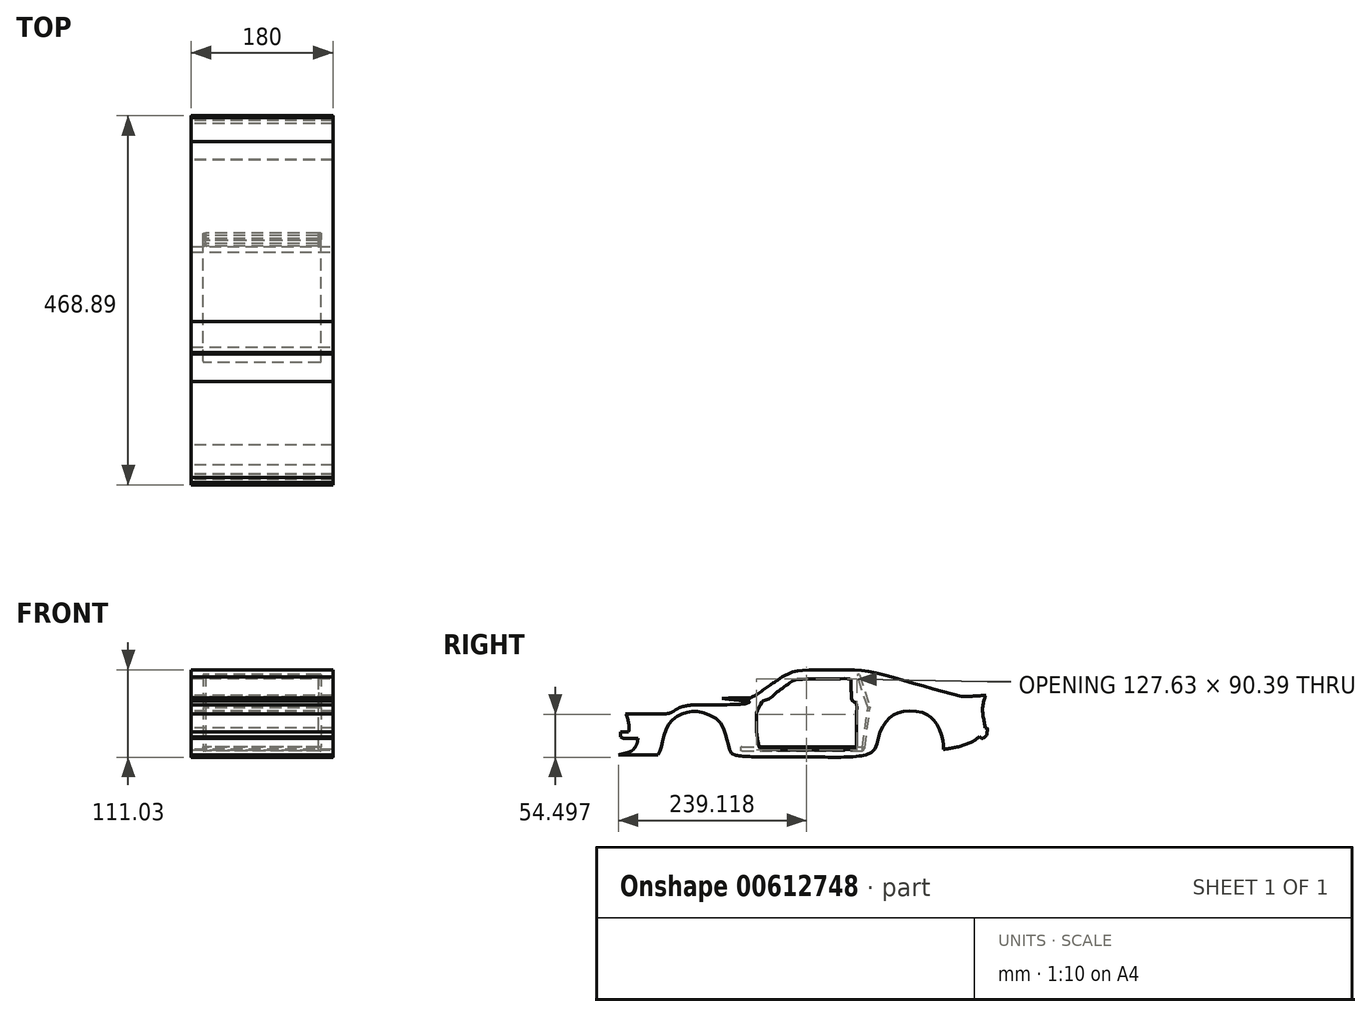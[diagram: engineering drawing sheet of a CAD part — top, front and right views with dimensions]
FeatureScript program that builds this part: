
annotation { "Feature Type Name" : "Feature", "Feature Type Description" : "" }
export const myFeature = defineFeature(function(context is Context, id is Id, definition is map)
    precondition{}
    {
        {
            var Q0;
            Q0=qCreatedBy(makeId("Right.planeOp"),FACE);
            var sketch = newSketch(context, id + "F0", { "sketchPlane" : qUnion([Q0])});
            skLineSegment(sketch, "E0", {"start": v(34.5, 1.2) * mm, "end": v(34.5, 56.2) * mm});
            skLineSegment(sketch, "E1", {"start": v(34.5, 56.2) * mm, "end": v(34.5, -53.8) * mm});
            skFitSpline(sketch, "E2", {"points": [v(-192.02, 5.62) * mm, v(-188.23, -1.97) * mm, v(-186.33, -8.9) * mm, v(-185.33, -17.74) * mm, v(-186.06, -22.02) * mm], "startDerivative": vector(14.34, -26.77) * mm, "endDerivative": vector(-3.15, -14.8) * mm});
            skLineSegment(sketch, "E3", {"start": v(-186.06, -22.02) * mm, "end": v(-150.06, -22.02) * mm});
            skLineSegment(sketch, "E4", {"start": v(-186.06, -22.02) * mm, "end": v(-196.06, -22.02) * mm});
            skLineSegment(sketch, "E5", {"start": v(-196.06, -22.02) * mm, "end": v(-196.06, -28.02) * mm});
            skLineSegment(sketch, "E6", {"start": v(-196.06, -28.02) * mm, "end": v(-192.6, -30.02) * mm});
            skLineSegment(sketch, "E7", {"start": v(-192.6, -30.02) * mm, "end": v(-152.6, -30.02) * mm});
            skFitSpline(sketch, "E8", {"points": [v(-189.69, 1.2) * mm, v(-143.65, 1.2) * mm, v(-132.51, 2.57) * mm, v(-124.9, 7.2) * mm, v(-118.52, 10.02) * mm, v(-106.8, 12.25) * mm, v(-95.05, 12.73) * mm, v(-67.03, 12.66) * mm, v(-45.8, 13.3) * mm, v(-38.33, 13.95) * mm, v(-33.02, 16.11) * mm, v(-30.86, 21.5) * mm], "startDerivative": vector(365.59, 0) * mm, "endDerivative": vector(6.51, 98.79) * mm});
            skLineSegment(sketch, "E9", {"start": v(-32.83, 21.62) * mm, "end": v(-30.86, 21.5) * mm});
            skLineSegment(sketch, "E10", {"start": v(-148.82, -50.9) * mm, "end": v(-203.82, -50.9) * mm});
            skFitSpline(sketch, "E11", {"points": [v(-203.82, -50.9) * mm, v(-201.8, -50.97) * mm, v(-195.54, -50.07) * mm, v(-184.25, -46.94) * mm, v(-179.78, -43.7) * mm, v(-175.75, -37.77) * mm, v(-174.19, -30.02) * mm], "startDerivative": vector(14.97, 20.7) * mm, "endDerivative": vector(5.44, 44.14) * mm});
            skFitSpline(sketch, "E12", {"points": [v(-192.6, -30.02) * mm, v(-190.74, -34.42) * mm, v(-187.5, -41.24) * mm, v(-184.25, -46.94) * mm], "startDerivative": vector(3.9, -14.04) * mm, "endDerivative": vector(12.4, -22.87) * mm});
            skFitSpline(sketch, "E13", {"points": [v(-191.23, -30.02) * mm, v(-189.5, -34.04) * mm, v(-185.58, -40.09) * mm, v(-179.78, -43.7) * mm], "startDerivative": vector(6.31, -12.78) * mm, "endDerivative": vector(21.2, -4.61) * mm});
            skFitSpline(sketch, "E14", {"points": [v(-173.44, -22.02) * mm, v(-172.32, -17.3) * mm, v(-173.44, -10.15) * mm, v(-176.23, -2.55) * mm, v(-178.58, 1.2) * mm], "startDerivative": vector(6.87, 20.01) * mm, "endDerivative": vector(-11.1, 15.63) * mm});
            skFitSpline(sketch, "E15", {"points": [v(-164.83, -22.02) * mm, v(-161.47, -19.43) * mm, v(-159.12, -13.17) * mm, v(-159.24, -5.46) * mm, v(-160.13, 1.18) * mm], "startDerivative": vector(17.5, 10.07) * mm, "endDerivative": vector(-3.71, 25.15) * mm});
            skFitSpline(sketch, "E16", {"points": [v(-148.82, -50.9) * mm, v(-144.92, -43.03) * mm, v(-142.13, -29.94) * mm, v(-136.76, -14.85) * mm, v(-126.59, -3.44) * mm, v(-114.17, 2.26) * mm, v(-102.43, 4.27) * mm, v(-84.65, 0.36) * mm, v(-69.45, -10.71) * mm, v(-62.3, -26.37) * mm, v(-59.38, -38.44) * mm, v(-56.36, -47.83) * mm, v(-45.3, -52.3) * mm, v(-13.05, -53.35) * mm, v(7.6, -53.58) * mm], "startDerivative": vector(73.15, 160.48) * mm, "endDerivative": vector(240.73, -3.86) * mm});
            skFitSpline(sketch, "E17", {"points": [v(213.63, -43.94) * mm, v(234.09, -40.23) * mm, v(253.22, -32.62) * mm, v(262, -26.18) * mm, v(266.1, -24.23) * mm, v(266.88, -17) * mm, v(265.12, -6.27) * mm, v(263.56, 7.6) * mm, v(265.71, 19.51) * mm, v(267.62, 24.74) * mm], "startDerivative": vector(137.64, 17.09) * mm, "endDerivative": vector(24.1, 59.58) * mm});
            skFitSpline(sketch, "E18", {"points": [v(266.88, -17) * mm, v(265.12, -17) * mm, v(262.4, -17) * mm, v(258.68, -17) * mm, v(257.15, -18.37) * mm, v(257.15, -21.73) * mm, v(258.3, -25.76) * mm, v(260.84, -28.8) * mm, v(262.9, -30.02) * mm, v(265.77, -28.87) * mm, v(268.4, -26.17) * mm, v(269.3, -22.64) * mm, v(269.3, -17) * mm, v(266.88, -17) * mm]});
            skFitSpline(sketch, "E19", {"points": [v(7.6, -53.58) * mm, v(26.53, -53.46) * mm, v(61.93, -53.8) * mm, v(115.2, -50.9) * mm, v(127.52, -41.9) * mm, v(133.08, -22.93) * mm, v(142.48, -7.27) * mm, v(153.5, 1.2) * mm, v(169.34, 5.17) * mm, v(191.58, 1.2) * mm, v(199.59, -5.06) * mm, v(207.48, -15.62) * mm, v(213.05, -32.57) * mm, v(213.63, -43.94) * mm], "startDerivative": vector(235.53, -2.28) * mm, "endDerivative": vector(-18.69, -186.2) * mm});
            skFitSpline(sketch, "E20", {"points": [v(-30.86, 21.5) * mm, v(-26.93, 19.51) * mm, v(-23.3, 19.33) * mm, v(-19.78, 19.51) * mm, v(-16.02, 21.5) * mm, v(10.62, 41.85) * mm, v(14.97, 44.81) * mm, v(15.38, 46.5) * mm, v(13.58, 47.43) * mm, v(8.48, 47.77) * mm], "startDerivative": vector(38.14, -25.76) * mm, "endDerivative": vector(-51.85, 1.69) * mm});
            skFitSpline(sketch, "E21", {"points": [v(-15.26, 17.54) * mm, v(-19.76, 11.3) * mm, v(-23.08, 3.29) * mm, v(-23.86, -5.7) * mm, v(-23.47, -19.36) * mm, v(-22.3, -29.9) * mm, v(-21.12, -37.12) * mm, v(-19.76, -42.4) * mm, v(-11.17, -44.15) * mm, v(14.6, -44.54) * mm, v(53.99, -44.53) * mm, v(82.73, -44.34) * mm, v(98.09, -43.75) * mm, v(102.52, -41.2) * mm, v(103.54, -32.58) * mm, v(103.6, 5.18) * mm, v(102.56, 15.34) * mm, v(98.37, 17.49) * mm, v(96.74, 26.5) * mm, v(96.66, 36.35) * mm, v(96.66, 42.91) * mm, v(95.68, 44.96) * mm, v(81.56, 45.78) * mm, v(56.6, 45.62) * mm, v(29.28, 44.8) * mm, v(21.8, 42.75) * mm, v(11.47, 35.2) * mm, v(0.72, 27.32) * mm, v(-8.64, 19.69) * mm, v(-15.26, 17.54) * mm]});
            skFitSpline(sketch, "E22", {"points": [v(8.48, 47.77) * mm, v(14.97, 51.2) * mm, v(26.65, 55.33) * mm, v(46.94, 56.85) * mm, v(97.46, 56.85) * mm, v(127.97, 53.26) * mm, v(181.98, 38.26) * mm, v(236.6, 23.3) * mm], "startDerivative": vector(84.82, 47.6) * mm, "endDerivative": vector(279.07, -65.23) * mm});
            skFitSpline(sketch, "E23", {"points": [v(8.48, 47.77) * mm, v(1.78, 43.11) * mm, v(-5.74, 38.1) * mm, v(-14.94, 31.55) * mm, v(-24.27, 25.14) * mm, v(-30.86, 21.5) * mm], "startDerivative": vector(-35.57, -25.23) * mm, "endDerivative": vector(-34.63, -24.08) * mm});
            skArc(sketch, "E24", {"start": v(224.04, -42.4) * mm, "mid": v(171.31, 15.22) * mm, "end": v(119.33, -43.08) * mm});
            skLineSegment(sketch, "E25", {"start": v(119.33, -43.08) * mm, "end": v(115.2, -50.9) * mm});
            skArc(sketch, "E26", {"start": v(-49.73, -51.5) * mm, "mid": v(-98.4, 12.55) * mm, "end": v(-153.36, -46.19) * mm});
            skLineSegment(sketch, "E27", {"start": v(-153.36, -46.19) * mm, "end": v(-148.82, -50.9) * mm});
            skFitSpline(sketch, "E28", {"points": [v(-192.02, 5.62) * mm, v(-171.85, 12.08) * mm, v(-144.7, 17.14) * mm, v(-106.6, 19.87) * mm, v(-67.7, 20.83) * mm, v(-46.55, 21.45) * mm, v(-32.83, 21.62) * mm], "startDerivative": vector(129.5, 46.92) * mm, "endDerivative": vector(108.9, 1.61) * mm});
            skLineSegment(sketch, "E29", {"start": v(-15.26, 17.54) * mm, "end": v(-31.31, 19.04) * mm});
            skFitSpline(sketch, "E30", {"points": [v(267.62, 24.74) * mm, v(236.6, 23.3) * mm, v(154.17, 23.3) * mm, v(117.95, 18.48) * mm, v(68.92, 14.9) * mm, v(0.95, 15.46) * mm, v(-67.7, 20.83) * mm], "startDerivative": vector(-203.68, -16.4) * mm, "endDerivative": vector(-404.49, 46.26) * mm});
            skLineSegment(sketch, "E31", {"start": v(-67.7, 20.83) * mm, "end": v(-32.83, 21.62) * mm});
            skLineSegment(sketch, "E32", {"start": v(117.27, -47) * mm, "end": v(-48.93, -47) * mm});
            skLineSegment(sketch, "E33", {"start": v(240.83, 54.27) * mm, "end": v(272.77, 56.66) * mm});
            skLineSegment(sketch, "E34", {"start": v(272.77, 56.66) * mm, "end": v(264.67, 50.23) * mm});
            skLineSegment(sketch, "E35", {"start": v(264.67, 50.23) * mm, "end": v(242.9, 50.23) * mm});
            skLineSegment(sketch, "E36", {"start": v(242.9, 50.23) * mm, "end": v(240.83, 54.27) * mm});
            skLineSegment(sketch, "E37", {"start": v(236.6, 23.3) * mm, "end": v(253.78, 55.24) * mm});
            skPoint(sketch, "E37.endSnap0", {"position": v(253.78, 50.23) * mm});
            skLineSegment(sketch, "E38", {"start": v(246.23, 23.46) * mm, "end": v(263.74, 55.99) * mm});
            skLineSegment(sketch, "E39", {"start": v(-192.02, 5.62) * mm, "end": v(-213.66, -3) * mm});
            skSolve(sketch);
        }
        {
            var Q0;
            {var subQ0=sQuery(id+"F0.wireOp",EDGE,"E15");Q0=makeQuery(id+"F0.imprint","IMPRINT",FACE,{"disambiguationData":[TD([[makeQuery(id+"F0.imprint","IMPRINT",EDGE,{"derivedFrom":subQ0}),-1.0]])]});}
            var Q1;
            {var subQ0=sQuery(id+"F0.wireOp",EDGE,"E14");Q1=makeQuery(id+"F0.imprint","IMPRINT",FACE,{"disambiguationData":[TD([[makeQuery(id+"F0.imprint","IMPRINT",EDGE,{"derivedFrom":subQ0}),-1.0]])]});}
            var Q2;
            {var subQ0=sQuery(id+"F0.wireOp",EDGE,"E4");Q2=makeQuery(id+"F0.imprint","IMPRINT",FACE,{"disambiguationData":[TD([[makeQuery(id+"F0.imprint","IMPRINT",EDGE,{"derivedFrom":subQ0}),1.0]])]});}
            var Q3;
            {var subQ5=sQuery(id+"F0.wireOp",EDGE,"E21");var subQ6=sQuery(id+"F0.wireOp",EDGE,"E1");var subQ7=makeQuery(id+"F0.imprint","INTERSECT",VERTEX,{"disambiguationData":[OD(1.0)],"derivedFrom":[subQ6,subQ5]});Q3=makeQuery(id+"F0.imprint","IMPRINT",FACE,{"disambiguationData":[TD([[makeQuery(id+"F0.imprint","IMPRINT",EDGE,{"disambiguationData":[TD([[subQ7,-1.0]])],"derivedFrom":subQ6}),-1.0]])]});}
            var Q4;
            {var subQ0=sQuery(id+"F0.wireOp",EDGE,"E1");var subQ1=makeQuery(id+"F0.imprint","IMPRINT",VERTEX,{"derivedFrom":subQ0});Q4=makeQuery(id+"F0.imprint","IMPRINT",FACE,{"disambiguationData":[TD([[makeQuery(id+"F0.imprint","IMPRINT",EDGE,{"disambiguationData":[TD([[subQ1,1.0]])],"derivedFrom":subQ0}),-1.0]])]});}
            var Q5;
            {var subQ0=sQuery(id+"F0.wireOp",EDGE,"E1");var subQ1=makeQuery(id+"F0.imprint","IMPRINT",VERTEX,{"derivedFrom":subQ0});Q5=makeQuery(id+"F0.imprint","IMPRINT",FACE,{"disambiguationData":[TD([[makeQuery(id+"F0.imprint","IMPRINT",EDGE,{"disambiguationData":[TD([[subQ1,1.0]])],"derivedFrom":subQ0}),1.0]])]});}
            var Q6;
            {var subQ0=sQuery(id+"F0.wireOp",EDGE,"E19");var subQ1=sQuery(id+"F0.wireOp",EDGE,"E1");var subQ2=makeQuery(id+"F0.imprint","INTERSECT",VERTEX,{"derivedFrom":[subQ1,subQ0]});Q6=makeQuery(id+"F0.imprint","IMPRINT",FACE,{"disambiguationData":[TD([[makeQuery(id+"F0.imprint","IMPRINT",EDGE,{"disambiguationData":[TD([[subQ2,1.0]])],"derivedFrom":subQ1}),1.0]])]});}
            var Q7;
            {var subQ5=sQuery(id+"F0.wireOp",EDGE,"E19");var subQ7=sQuery(id+"F0.wireOp",EDGE,"E1");var subQ8=makeQuery(id+"F0.imprint","INTERSECT",VERTEX,{"derivedFrom":[subQ7,subQ5]});Q7=makeQuery(id+"F0.imprint","IMPRINT",FACE,{"disambiguationData":[TD([[makeQuery(id+"F0.imprint","IMPRINT",EDGE,{"disambiguationData":[TD([[subQ8,1.0]])],"derivedFrom":subQ7}),-1.0]])]});}
            var Q8;
            {var subQ11=sQuery(id+"F0.wireOp",EDGE,"E24");Q8=makeQuery(id+"F0.imprint","IMPRINT",FACE,{"disambiguationData":[TD([[makeQuery(id+"F0.imprint","IMPRINT",EDGE,{"derivedFrom":subQ11}),-1.0]])]});}
            var Q9;
            {var subQ5=sQuery(id+"F0.wireOp",EDGE,"E20");Q9=makeQuery(id+"F0.imprint","IMPRINT",FACE,{"disambiguationData":[TD([[makeQuery(id+"F0.imprint","IMPRINT",EDGE,{"derivedFrom":subQ5}),-1.0]])]});}
            var Q10;
            {var subQ0=sQuery(id+"F0.wireOp",EDGE,"E21");var subQ1=sQuery(id+"F0.wireOp",EDGE,"E1");var subQ2=makeQuery(id+"F0.imprint","INTERSECT",VERTEX,{"disambiguationData":[OD(0.0)],"derivedFrom":[subQ1,subQ0]});Q10=makeQuery(id+"F0.imprint","IMPRINT",FACE,{"disambiguationData":[TD([[makeQuery(id+"F0.imprint","IMPRINT",EDGE,{"disambiguationData":[TD([[subQ2,-1.0]])],"derivedFrom":subQ1}),1.0]])]});}
            var Q11;
            {var subQ4=sQuery(id+"F0.wireOp",EDGE,"E9");Q11=makeQuery(id+"F0.imprint","IMPRINT",FACE,{"disambiguationData":[TD([[makeQuery(id+"F0.imprint","IMPRINT",EDGE,{"derivedFrom":subQ4}),-1.0]])]});}
            var Q12;
            {var subQ0=sQuery(id+"F0.wireOp",EDGE,"E21");var subQ1=sQuery(id+"F0.wireOp",EDGE,"E1");var subQ2=makeQuery(id+"F0.imprint","INTERSECT",VERTEX,{"disambiguationData":[OD(0.0)],"derivedFrom":[subQ1,subQ0]});Q12=makeQuery(id+"F0.imprint","IMPRINT",FACE,{"disambiguationData":[TD([[makeQuery(id+"F0.imprint","IMPRINT",EDGE,{"disambiguationData":[TD([[subQ2,-1.0]])],"derivedFrom":subQ1}),-1.0]])]});}
            var Q13;
            {var subQ0=sQuery(id+"F0.wireOp",EDGE,"E18");var subQ1=sQuery(id+"F0.wireOp",EDGE,"E17");var subQ2=makeQuery(id+"F0.imprint","INTERSECT",VERTEX,{"disambiguationData":[OD(0.0)],"derivedFrom":[subQ1,subQ0]});Q13=makeQuery(id+"F0.imprint","IMPRINT",FACE,{"disambiguationData":[TD([[makeQuery(id+"F0.imprint","IMPRINT",EDGE,{"disambiguationData":[TD([[subQ2,-1.0]])],"derivedFrom":subQ1}),1.0]])]});}
            var Q14;
            {var subQ0=sQuery(id+"F0.wireOp",EDGE,"E18");var subQ1=sQuery(id+"F0.wireOp",EDGE,"E17");var subQ2=makeQuery(id+"F0.imprint","INTERSECT",VERTEX,{"disambiguationData":[OD(0.0)],"derivedFrom":[subQ1,subQ0]});Q14=makeQuery(id+"F0.imprint","IMPRINT",FACE,{"disambiguationData":[TD([[makeQuery(id+"F0.imprint","IMPRINT",EDGE,{"disambiguationData":[TD([[subQ2,-1.0]])],"derivedFrom":subQ1}),-1.0]])]});}
            var Q15;
            {var subQ0=sQuery(id+"F0.wireOp",EDGE,"E29");Q15=makeQuery(id+"F0.imprint","IMPRINT",FACE,{"disambiguationData":[TD([[makeQuery(id+"F0.imprint","IMPRINT",EDGE,{"derivedFrom":subQ0}),1.0]])]});}
            var Q16;
            {var subQ5=sQuery(id+"F0.wireOp",EDGE,"E27");Q16=makeQuery(id+"F0.imprint","IMPRINT",FACE,{"disambiguationData":[TD([[makeQuery(id+"F0.imprint","IMPRINT",EDGE,{"derivedFrom":subQ5}),-1.0]])]});}
            var Q17;
            {var subQ4=sQuery(id+"F0.wireOp",EDGE,"E27");Q17=makeQuery(id+"F0.imprint","IMPRINT",FACE,{"disambiguationData":[TD([[makeQuery(id+"F0.imprint","IMPRINT",EDGE,{"derivedFrom":subQ4}),1.0]])]});}
            var Q18;
            {var subQ0=sQuery(id+"F0.wireOp",EDGE,"E24");Q18=makeQuery(id+"F0.imprint","IMPRINT",FACE,{"disambiguationData":[TD([[makeQuery(id+"F0.imprint","IMPRINT",EDGE,{"derivedFrom":subQ0}),1.0]])]});}
            var Q19;
            {var subQ9=sQuery(id+"F0.wireOp",EDGE,"E28");Q19=makeQuery(id+"F0.imprint","IMPRINT",FACE,{"disambiguationData":[TD([[makeQuery(id+"F0.imprint","IMPRINT",EDGE,{"derivedFrom":subQ9}),-1.0]])]});}
            var Q20;
            {var subQ5=sQuery(id+"F0.wireOp",EDGE,"E14");Q20=makeQuery(id+"F0.imprint","IMPRINT",FACE,{"disambiguationData":[TD([[makeQuery(id+"F0.imprint","IMPRINT",EDGE,{"derivedFrom":subQ5}),1.0]])]});}
            var Q21;
            {var subQ0=sQuery(id+"F0.wireOp",EDGE,"E26");var subQ1=sQuery(id+"F0.wireOp",EDGE,"E8");var subQ2=makeQuery(id+"F0.imprint","INTERSECT",VERTEX,{"disambiguationData":[OD(1.0)],"derivedFrom":[subQ1,subQ0]});Q21=makeQuery(id+"F0.imprint","IMPRINT",FACE,{"disambiguationData":[TD([[makeQuery(id+"F0.imprint","IMPRINT",EDGE,{"disambiguationData":[TD([[subQ2,-1.0]])],"derivedFrom":subQ1}),-1.0]])]});}
            var Q22;
            Q22=makeQuery(id+"F0.imprint","IMPRINT",FACE,{"disambiguationData":[TD([[makeQuery(id+"F0.imprint","IMPRINT",EDGE,{"derivedFrom":sQuery(id+"F0.wireOp",EDGE,"E20")}),1.0]])]});
            extrude(context, id + "F1", {"entities" : qUnion([Q0, Q1, Q2, Q3, Q4, Q5, Q6, Q7, Q8, Q9, Q10, Q11, Q12, Q13, Q14, Q15, Q16, Q17, Q18, Q19, Q20, Q21, Q22]), "endBound" : BoundingType.SYMMETRIC, "depth" : 180 * mm, "offsetDistance" : 25 * mm});
        }
        {
            var Q0;
            Q0=qCreatedBy(makeId("Right.planeOp"),FACE);
            var sketch = newSketch(context, id + "F2", { "sketchPlane" : qUnion([Q0])});
            skLineSegment(sketch, "E40.bottom", {"start": v(-43.54, -46.1) * mm, "end": v(111, -46.1) * mm});
            skLineSegment(sketch, "E40.top", {"start": v(-43.54, -41.1) * mm, "end": v(111, -41.1) * mm});
            skLineSegment(sketch, "E40.left", {"start": v(-43.54, -46.1) * mm, "end": v(-43.54, -41.1) * mm});
            skLineSegment(sketch, "E40.right", {"start": v(111, -46.1) * mm, "end": v(111, -41.1) * mm});
            skLineSegment(sketch, "E41", {"start": v(111, -41.1) * mm, "end": v(117.75, 9.14) * mm});
            skLineSegment(sketch, "E42", {"start": v(117.75, 9.14) * mm, "end": v(104.27, 50.54) * mm});
            skLineSegment(sketch, "E43", {"start": v(104.27, 50.54) * mm, "end": v(107.12, 51.47) * mm});
            skLineSegment(sketch, "E44", {"start": v(107.12, 51.47) * mm, "end": v(120.6, 10.07) * mm});
            skLineSegment(sketch, "E45", {"start": v(111, -41.1) * mm, "end": v(113.98, -41.5) * mm});
            skLineSegment(sketch, "E46", {"start": v(113.98, -41.5) * mm, "end": v(120.73, 8.74) * mm});
            skLineSegment(sketch, "E47", {"start": v(117.75, 9.14) * mm, "end": v(120.6, 10.07) * mm});
            skLineSegment(sketch, "E48", {"start": v(117.75, 9.14) * mm, "end": v(120.73, 8.74) * mm});
            skLineSegment(sketch, "E49", {"start": v(120.6, 10.07) * mm, "end": v(120.73, 8.74) * mm});
            skLineSegment(sketch, "E50", {"start": v(111, -46.1) * mm, "end": v(113.98, -41.5) * mm});
            skLineSegment(sketch, "E51.bottom", {"start": v(-43.54, -41.1) * mm, "end": v(-40.54, -41.1) * mm});
            skLineSegment(sketch, "E51.top", {"start": v(-43.54, 13.9) * mm, "end": v(-40.54, 13.9) * mm});
            skLineSegment(sketch, "E51.left", {"start": v(-43.54, -41.1) * mm, "end": v(-43.54, 13.9) * mm});
            skLineSegment(sketch, "E51.right", {"start": v(-40.54, -41.1) * mm, "end": v(-40.54, 13.9) * mm});
            skLineSegment(sketch, "E52", {"start": v(-143.63, 15.68) * mm, "end": v(-143.63, -28.4) * mm});
            skLineSegment(sketch, "E53", {"start": v(-143.63, -28.4) * mm, "end": v(-123.33, -28.4) * mm});
            skLineSegment(sketch, "E54", {"start": v(-123.33, -28.4) * mm, "end": v(-112.9, -17.44) * mm});
            skLineSegment(sketch, "E55", {"start": v(-112.9, -17.44) * mm, "end": v(-85.4, -17.44) * mm});
            skLineSegment(sketch, "E56", {"start": v(-85.4, -17.44) * mm, "end": v(-43.54, -41.1) * mm});
            skLineSegment(sketch, "E57", {"start": v(-143.63, 15.68) * mm, "end": v(-43.54, 20.22) * mm});
            skLineSegment(sketch, "E58", {"start": v(-43.54, 20.22) * mm, "end": v(-43.54, 13.9) * mm});
            skSolve(sketch);
        }
        {
            var Q0;
            Q0=makeQuery(id+"F2.imprint","IMPRINT",FACE,{"disambiguationData":[TD([[makeQuery(id+"F2.imprint","IMPRINT",EDGE,{"derivedFrom":sQuery(id+"F2.wireOp",EDGE,"E40.bottom")}),1.0]])]});
            var Q1;
            Q1=makeQuery(id+"F2.imprint","IMPRINT",FACE,{"disambiguationData":[TD([[makeQuery(id+"F2.imprint","IMPRINT",EDGE,{"derivedFrom":sQuery(id+"F2.wireOp",EDGE,"E51.bottom")}),1.0]])]});
            var Q2;
            Q2=makeQuery(id+"F2.imprint","IMPRINT",FACE,{"disambiguationData":[TD([[makeQuery(id+"F2.imprint","IMPRINT",EDGE,{"derivedFrom":sQuery(id+"F2.wireOp",EDGE,"E40.right")}),-1.0]])]});
            var Q3;
            Q3=makeQuery(id+"F2.imprint","IMPRINT",FACE,{"disambiguationData":[TD([[makeQuery(id+"F2.imprint","IMPRINT",EDGE,{"derivedFrom":sQuery(id+"F2.wireOp",EDGE,"E41")}),-1.0]])]});
            var Q4;
            Q4=makeQuery(id+"F2.imprint","IMPRINT",FACE,{"disambiguationData":[TD([[makeQuery(id+"F2.imprint","IMPRINT",EDGE,{"derivedFrom":sQuery(id+"F2.wireOp",EDGE,"E42")}),-1.0]])]});
            var Q5;
            Q5=makeQuery(id+"F2.imprint","IMPRINT",FACE,{"disambiguationData":[TD([[makeQuery(id+"F2.imprint","IMPRINT",EDGE,{"derivedFrom":sQuery(id+"F2.wireOp",EDGE,"E47")}),-1.0]])]});
            extrude(context, id + "F3", {"entities" : qUnion([Q0, Q1, Q2, Q3, Q4, Q5]), "endBound" : BoundingType.SYMMETRIC, "depth" : 150 * mm, "offsetDistance" : 25 * mm});
        }
        {
            var Q0;
            Q0=makeQuery(id+"F2.imprint","IMPRINT",FACE,{"disambiguationData":[TD([[makeQuery(id+"F2.imprint","IMPRINT",EDGE,{"derivedFrom":sQuery(id+"F2.wireOp",EDGE,"E51.bottom")}),1.0]])]});
            var Q1;
            Q1=makeQuery(id+"F2.imprint","IMPRINT",FACE,{"disambiguationData":[TD([[makeQuery(id+"F2.imprint","IMPRINT",EDGE,{"derivedFrom":sQuery(id+"F2.wireOp",EDGE,"E41")}),-1.0]])]});
            var Q2;
            Q2=makeQuery(id+"F2.imprint","IMPRINT",FACE,{"disambiguationData":[TD([[makeQuery(id+"F2.imprint","IMPRINT",EDGE,{"derivedFrom":sQuery(id+"F2.wireOp",EDGE,"E40.right")}),-1.0]])]});
            var Q3;
            Q3=makeQuery(id+"F2.imprint","IMPRINT",FACE,{"disambiguationData":[TD([[makeQuery(id+"F2.imprint","IMPRINT",EDGE,{"derivedFrom":sQuery(id+"F2.wireOp",EDGE,"E47")}),-1.0]])]});
            var Q4;
            Q4=makeQuery(id+"F2.imprint","IMPRINT",FACE,{"disambiguationData":[TD([[makeQuery(id+"F2.imprint","IMPRINT",EDGE,{"derivedFrom":sQuery(id+"F2.wireOp",EDGE,"E42")}),-1.0]])]});
            extrude(context, id + "F4", {"entities" : qUnion([Q0, Q1, Q2, Q3, Q4]), "operationType" : NewBodyOperationType.REMOVE, "endBound" : BoundingType.SYMMETRIC, "depth" : 144 * mm, "offsetDistance" : 25 * mm});
        }
        {
            var Q0;
            Q0=makeQuery(id+"F3.opExtrude","CAP_EDGE",EDGE,{"disambiguationData":[OSD([sQuery(id+"F2.wireOp",EDGE,"E42")])],"isStart":false});
            var Q1;
            Q1=makeQuery(id+"F3.opExtrude","CAP_EDGE",EDGE,{"disambiguationData":[OSD([sQuery(id+"F2.wireOp",EDGE,"E44")])],"isStart":false});
            var Q2;
            Q2=makeQuery(id+"F4.boolean.opBoolean","COPY",EDGE,{"derivedFrom":makeQuery(id+"F4.opExtrude","CAP_EDGE",EDGE,{"disambiguationData":[OSD([sQuery(id+"F2.wireOp",EDGE,"E42")])],"isStart":false})});
            var Q3;
            Q3=makeQuery(id+"F4.boolean.opBoolean","COPY",EDGE,{"derivedFrom":makeQuery(id+"F4.opExtrude","CAP_EDGE",EDGE,{"disambiguationData":[OSD([sQuery(id+"F2.wireOp",EDGE,"E44")])],"isStart":false})});
            var Q4;
            Q4=makeQuery(id+"F3.opExtrude","CAP_EDGE",EDGE,{"disambiguationData":[OSD([sQuery(id+"F2.wireOp",EDGE,"E46")])],"isStart":false});
            var Q5;
            Q5=makeQuery(id+"F3.opExtrude","CAP_EDGE",EDGE,{"disambiguationData":[OSD([sQuery(id+"F2.wireOp",EDGE,"E41")])],"isStart":false});
            var Q6;
            Q6=makeQuery(id+"F4.boolean.opBoolean","COPY",EDGE,{"derivedFrom":makeQuery(id+"F4.opExtrude","CAP_EDGE",EDGE,{"disambiguationData":[OSD([sQuery(id+"F2.wireOp",EDGE,"E46")])],"isStart":false})});
            var Q7;
            Q7=makeQuery(id+"F4.boolean.opBoolean","COPY",EDGE,{"derivedFrom":makeQuery(id+"F4.opExtrude","CAP_EDGE",EDGE,{"disambiguationData":[OSD([sQuery(id+"F2.wireOp",EDGE,"E41")])],"isStart":false})});
            var Q8;
            Q8=makeQuery(id+"F3.opExtrude","CAP_EDGE",EDGE,{"disambiguationData":[OSD([sQuery(id+"F2.wireOp",EDGE,"E40.left"),sQuery(id+"F2.wireOp",EDGE,"E51.left")])],"isStart":false});
            var Q9;
            Q9=makeQuery(id+"F4.boolean.opBoolean","COPY",EDGE,{"derivedFrom":makeQuery(id+"F4.opExtrude","CAP_EDGE",EDGE,{"disambiguationData":[OSD([sQuery(id+"F2.wireOp",EDGE,"E51.left")])],"isStart":false})});
            var Q10;
            Q10=makeQuery(id+"F3.opExtrude","CAP_EDGE",EDGE,{"disambiguationData":[OSD([sQuery(id+"F2.wireOp",EDGE,"E51.right")])],"isStart":false});
            var Q11;
            Q11=makeQuery(id+"F4.boolean.opBoolean","COPY",EDGE,{"derivedFrom":makeQuery(id+"F4.opExtrude","CAP_EDGE",EDGE,{"disambiguationData":[OSD([sQuery(id+"F2.wireOp",EDGE,"E51.right")])],"isStart":false})});
            var Q12;
            Q12=makeQuery(id+"F4.boolean.opBoolean","COPY",EDGE,{"derivedFrom":makeQuery(id+"F4.opExtrude","CAP_EDGE",EDGE,{"disambiguationData":[OSD([sQuery(id+"F2.wireOp",EDGE,"E51.right")])],"isStart":true})});
            var Q13;
            Q13=makeQuery(id+"F4.boolean.opBoolean","COPY",EDGE,{"derivedFrom":makeQuery(id+"F4.opExtrude","CAP_EDGE",EDGE,{"disambiguationData":[OSD([sQuery(id+"F2.wireOp",EDGE,"E44")])],"isStart":true})});
            var Q14;
            Q14=makeQuery(id+"F3.opExtrude","CAP_EDGE",EDGE,{"disambiguationData":[OSD([sQuery(id+"F2.wireOp",EDGE,"E44")])],"isStart":true});
            var Q15;
            Q15=makeQuery(id+"F4.boolean.opBoolean","COPY",EDGE,{"derivedFrom":makeQuery(id+"F4.opExtrude","CAP_EDGE",EDGE,{"disambiguationData":[OSD([sQuery(id+"F2.wireOp",EDGE,"E42")])],"isStart":true})});
            var Q16;
            Q16=makeQuery(id+"F4.boolean.opBoolean","COPY",EDGE,{"derivedFrom":makeQuery(id+"F4.opExtrude","CAP_EDGE",EDGE,{"disambiguationData":[OSD([sQuery(id+"F2.wireOp",EDGE,"E41")])],"isStart":true})});
            var Q17;
            Q17=makeQuery(id+"F3.opExtrude","CAP_EDGE",EDGE,{"disambiguationData":[OSD([sQuery(id+"F2.wireOp",EDGE,"E46")])],"isStart":true});
            var Q18;
            Q18=makeQuery(id+"F4.boolean.opBoolean","COPY",EDGE,{"derivedFrom":makeQuery(id+"F4.opExtrude","CAP_EDGE",EDGE,{"disambiguationData":[OSD([sQuery(id+"F2.wireOp",EDGE,"E46")])],"isStart":true})});
            var Q19;
            Q19=makeQuery(id+"F4.boolean.opBoolean","COPY",EDGE,{"derivedFrom":makeQuery(id+"F4.opExtrude","CAP_EDGE",EDGE,{"disambiguationData":[OSD([sQuery(id+"F2.wireOp",EDGE,"E51.left")])],"isStart":true})});
            var Q20;
            Q20=makeQuery(id+"F3.opExtrude","CAP_EDGE",EDGE,{"disambiguationData":[OSD([sQuery(id+"F2.wireOp",EDGE,"E51.right")])],"isStart":true});
            var Q21;
            Q21=makeQuery(id+"F3.opExtrude","CAP_EDGE",EDGE,{"disambiguationData":[OSD([sQuery(id+"F2.wireOp",EDGE,"E40.left"),sQuery(id+"F2.wireOp",EDGE,"E51.left")])],"isStart":true});
            var Q22;
            Q22=makeQuery(id+"F3.opExtrude","CAP_EDGE",EDGE,{"disambiguationData":[OSD([sQuery(id+"F2.wireOp",EDGE,"E41")])],"isStart":true});
            var Q23;
            Q23=makeQuery(id+"F3.opExtrude","CAP_EDGE",EDGE,{"disambiguationData":[OSD([sQuery(id+"F2.wireOp",EDGE,"E42")])],"isStart":true});
            fillet(context, id + "F5", {"entities" : qUnion([Q0, Q1, Q2, Q3, Q4, Q5, Q6, Q7, Q8, Q9, Q10, Q11, Q12, Q13, Q14, Q15, Q16, Q17, Q18, Q19, Q20, Q21, Q22, Q23]), "radius" : 1.5 * mm, "tangentPropagation" : true, "allowEdgeOverflow" : false});
        }
    });
